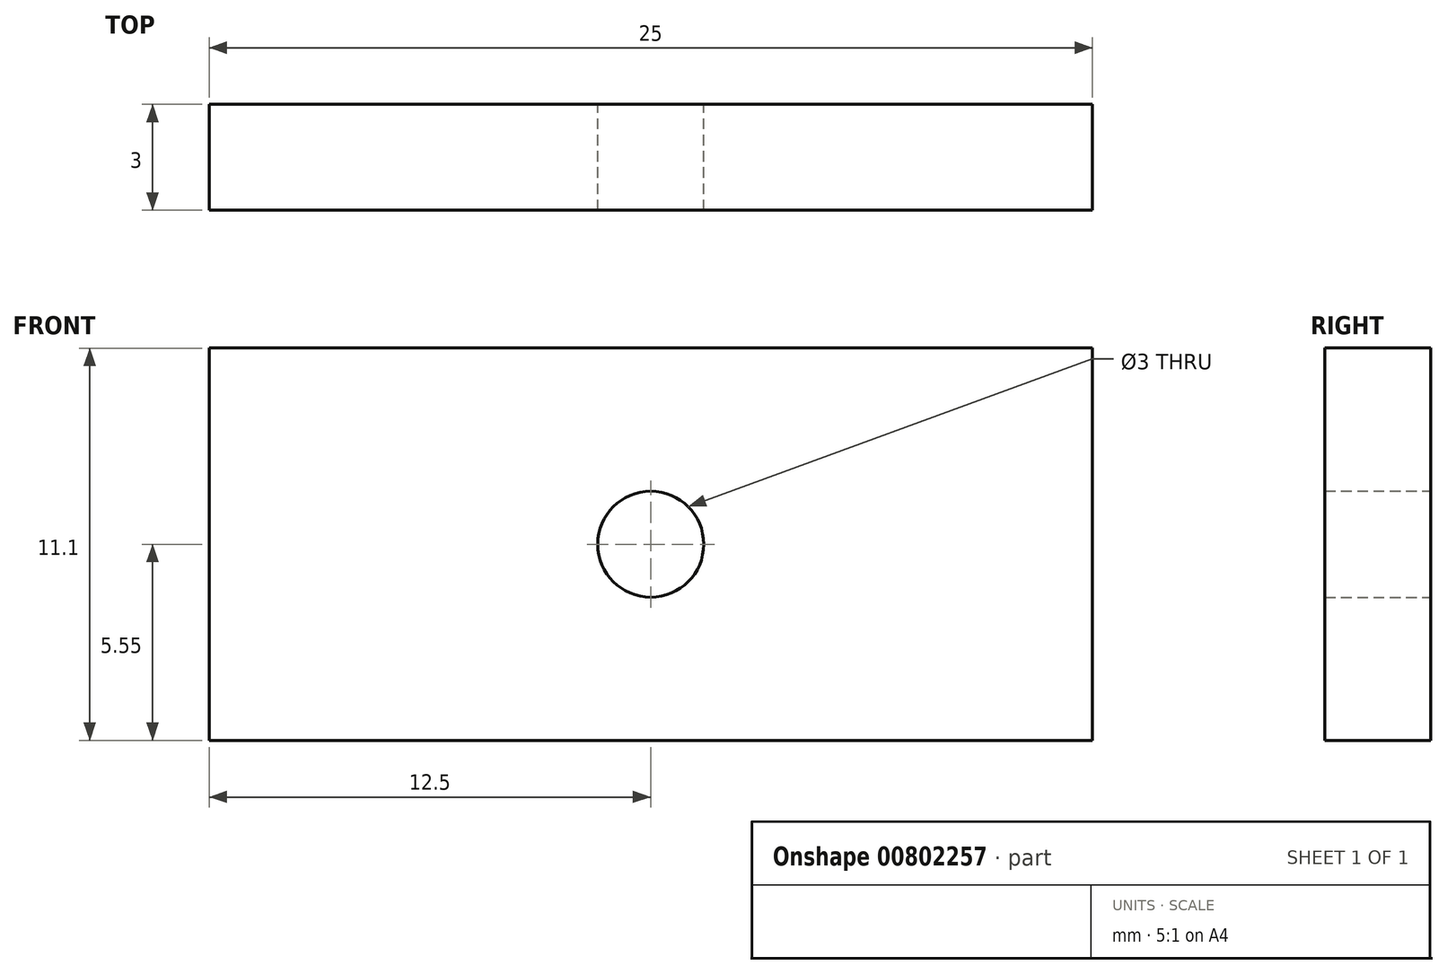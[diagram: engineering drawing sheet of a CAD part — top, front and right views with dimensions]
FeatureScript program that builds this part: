
annotation { "Feature Type Name" : "Feature", "Feature Type Description" : "" }
export const myFeature = defineFeature(function(context is Context, id is Id, definition is map)
    precondition{}
    {
        {
            var Q0;
            Q0=qCreatedBy(makeId("Front.planeOp"),FACE);
            var sketch = newSketch(context, id + "F0", { "sketchPlane" : qUnion([Q0])});
            skLineSegment(sketch, "E0.bottom", {"start": v(-12.5, 5.55) * mm, "end": v(12.5, 5.55) * mm});
            skLineSegment(sketch, "E0.top", {"start": v(-12.5, -5.56) * mm, "end": v(12.5, -5.56) * mm});
            skLineSegment(sketch, "E0.left", {"start": v(-12.5, 5.55) * mm, "end": v(-12.5, -5.56) * mm});
            skLineSegment(sketch, "E0.right", {"start": v(12.5, 5.55) * mm, "end": v(12.5, -5.56) * mm});
            skPoint(sketch, "E0.middle", {"position": v(0, 0) * mm});
            skCircle(sketch, "E1", {"center": v(0, 0) * mm, "radius": 1.5 * mm});
            skSolve(sketch);
        }
        {
            var Q0;
            Q0 = qSketchRegion(id + "F0", true);
            extrude(context, id + "F1", {"entities" : qUnion([Q0]), "depth" : 3 * mm, "offsetDistance" : 25 * mm});
        }
    });
